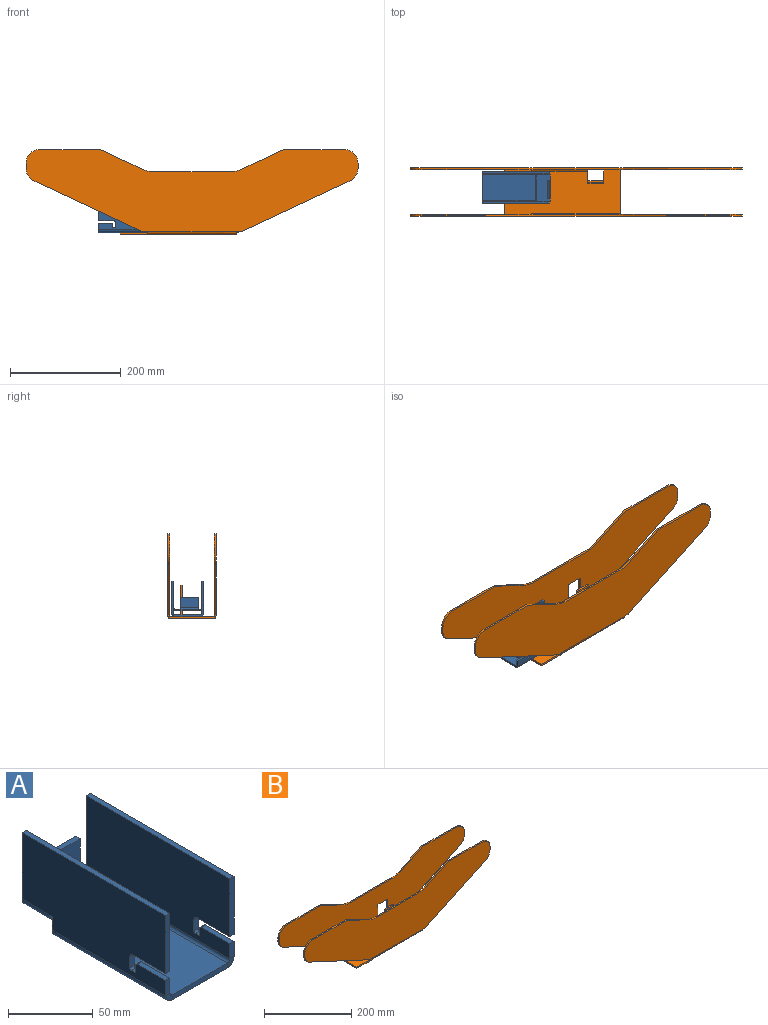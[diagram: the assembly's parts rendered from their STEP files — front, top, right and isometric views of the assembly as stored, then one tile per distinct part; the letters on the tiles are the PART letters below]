
ASSEMBLY  parts=2 mates=1
PART A: 69 faces, bbox 57x123.5x63.5 mm
  f0: cylinder r=1.5mm len=3.5mm, axis (1,0,0), area 8.2mm2, adj f1,f14,f15,f16
  f1: plane 4.5x3.5mm, normal (0,1,0), area 15.7mm2, adj f0,f2,f15,f16
  f2: cylinder r=1mm len=3.5mm, axis (1,0,0), area 5.5mm2, adj f1,f3,f15,f16
  f3: plane 3.5x3mm, normal (0,0,1), area 10.5mm2, adj f2,f4,f15,f16
  f4: cylinder r=1mm len=3.5mm, axis (1,0,0), area 5.5mm2, adj f3,f5,f15,f16
  f5: plane 8x3.5mm, normal (0,-1,0), area 28mm2, adj f4,f6,f15,f16
  f6: cylinder r=3mm len=3.5mm, axis (1,0,0), area 16.5mm2, adj f5,f7,f15,f16
  f7: plane 27x3.5mm, normal (0,0,-1), area 94.5mm2, adj f6,f8,f15,f16
  f8: plane 41.92x3.5mm, normal (0,-1,0), area 146.7mm2, adj f7,f9,f15,f16
  f9: plane 120x3.5mm, normal (0,0,1), area 420mm2, adj f8,f10,f15,f16
  f10: plane 48x3.5mm, normal (0,1,0), area 168mm2, adj f9,f15,f16,f66
  f11: plane 3.5x2mm, normal (0,0,-1), area 7mm2, adj f12,f15,f16,f65
  f12: plane 10x3.5mm, normal (0,1,0), area 35mm2, adj f11,f15,f16,f43
  f13: plane 11.08x3.5mm, normal (0,-1,0), area 38.8mm2, adj f14,f15,f16,f44
  f14: plane 23.5x3.5mm, normal (0,0,1), area 82.2mm2, adj f0,f13,f15,f16
  f15: plane 120x58mm, normal (-1,0,0), area 6526.9mm2, adj f0,f1,f2,f3,f4,f5,f6,f7
  f16: plane 120x58mm, normal (1,0,0), area 6526.9mm2, adj f0,f1,f2,f3,f4,f5,f6,f7
  f17: cylinder r=3mm len=3.5mm, axis (1,0,0), area 16.5mm2, adj f18,f32,f33,f34
  f18: plane 8x3.5mm, normal (0,-1,0), area 28mm2, adj f17,f19,f33,f34
  f19: cylinder r=1mm len=3.5mm, axis (1,0,0), area 5.5mm2, adj f18,f20,f33,f34
  f20: plane 3.5x3mm, normal (0,0,1), area 10.5mm2, adj f19,f21,f33,f34
  f21: cylinder r=1mm len=3.5mm, axis (1,0,0), area 5.5mm2, adj f20,f22,f33,f34
  f22: plane 4.5x3.5mm, normal (0,1,0), area 15.7mm2, adj f21,f23,f33,f34
  f23: cylinder r=1.5mm len=3.5mm, axis (1,0,0), area 8.2mm2, adj f22,f24,f33,f34
  f24: plane 23.5x3.5mm, normal (0,0,1), area 82.2mm2, adj f23,f25,f33,f34
  f25: plane 11.08x3.5mm, normal (0,-1,0), area 38.8mm2, adj f24,f33,f34,f40
  f26: plane 8.05x3.5mm, normal (0,1,0), area 28.2mm2, adj f27,f33,f34,f39
  f27: plane 3.5x2mm, normal (0,0,-1), area 7mm2, adj f26,f28,f33,f34
  f28: plane 23x3.5mm, normal (0,0,-1), area 80.5mm2, adj f27,f29,f33,f34
  f29: plane 49.95x3.5mm, normal (0,1,0), area 174.8mm2, adj f28,f30,f33,f34
  f30: plane 120x3.5mm, normal (0,0,1), area 420mm2, adj f29,f31,f33,f34
  f31: plane 41.92x3.5mm, normal (0,-1,0), area 146.7mm2, adj f30,f32,f33,f34
  f32: plane 27x3.5mm, normal (0,0,-1), area 94.5mm2, adj f17,f31,f33,f34
  f33: plane 120x58mm, normal (1,0,0), area 6575.6mm2, adj f17,f18,f19,f20,f21,f22,f23,f24
  f34: plane 120x58mm, normal (-1,0,0), area 6575.6mm2, adj f17,f18,f19,f20,f21,f22,f23,f24
  f35: plane 46x3.5mm, normal (0,-1,0), area 161mm2, adj f37,f38,f40,f44
  f36: plane 46x3.5mm, normal (0,1,0), area 161mm2, adj f37,f38,f39,f43
  f37: plane 95x46mm, normal (0,0,-1), area 4370mm2, adj f35,f36,f41,f45
  f38: plane 95x46mm, normal (0,0,1), area 4370mm2, adj f35,f36,f42,f46
  f39: plane 5.5x5.5mm, normal (0,1,0), area 20.6mm2, adj f26,f36,f41,f42
  f40: plane 5.5x5.5mm, normal (0,-1,0), area 20.6mm2, adj f25,f35,f41,f42
  f41: cylinder r=5.5mm len=95mm, axis (0,1,0), area 820.7mm2, adj f33,f37,f39,f40
  f42: cylinder r=2mm len=95mm, axis (0,1,0), area 298.5mm2, adj f34,f38,f39,f40
  f43: plane 5.5x5.5mm, normal (0,1,0), area 20.6mm2, adj f12,f36,f45,f46
  f44: plane 5.5x5.5mm, normal (0,-1,0), area 20.6mm2, adj f13,f35,f45,f46
  f45: cylinder r=5.5mm len=95mm, axis (0,1,0), area 820.7mm2, adj f15,f37,f43,f44
  f46: cylinder r=2mm len=95mm, axis (0,1,0), area 298.5mm2, adj f16,f38,f43,f44
  f47: plane 3.75x1.48mm, normal (-1,0,0), area 1.7mm2, adj f49,f54,f63
  f48: plane 3.75x1.48mm, normal (1,0,0), area 1.7mm2, adj f53,f54,f63
  f49: plane 5x3.5mm, normal (0,1,0), area 17.5mm2, adj f47,f50,f54,f55,f62
  f50: plane 3.5x1.75mm, normal (1,0,0), area 6.1mm2, adj f49,f51,f54,f55
  f51: plane 23x3.5mm, normal (1,0,0), area 80.5mm2, adj f50,f52,f54,f55
  f52: plane 47.95x3.5mm, normal (0,-1,0), area 167.8mm2, adj f51,f54,f55,f65
  f53: plane 10x3.5mm, normal (0,1,0), area 35mm2, adj f48,f54,f55,f56,f66
  f54: plane 47.95x24.75mm, normal (0,0,-1), area 1063.2mm2, adj f47,f48,f49,f50,f51,f52,f53,f63
  f55: plane 47.95x24.75mm, normal (0,0,1), area 1063.2mm2, adj f49,f50,f51,f52,f53,f56,f62,f64
  f56: plane 5.5x4.02mm, normal (-1,0,0), area 9.2mm2, adj f53,f55,f58,f63,f64
  f57: plane 19.5x3.5mm, normal (1,0,0), area 68.3mm2, adj f59,f60,f61,f62
  f58: plane 19.5x3.5mm, normal (-1,0,0), area 68.3mm2, adj f56,f59,f60,f61
  f59: plane 32.95x3.5mm, normal (0,0,1), area 115.3mm2, adj f57,f58,f60,f61
  f60: plane 32.95x19.5mm, normal (0,1,0), area 642.5mm2, adj f57,f58,f59,f63
  f61: plane 32.95x19.5mm, normal (0,-1,0), area 642.5mm2, adj f57,f58,f59,f64
  f62: plane 5.5x4.02mm, normal (1,0,0), area 9.2mm2, adj f49,f55,f57,f63,f64
  f63: cylinder r=5.5mm len=32.95mm, axis (1,0,0), area 284.7mm2, adj f47,f48,f54,f56,f60,f62
  f64: cylinder r=2mm len=32.95mm, axis (1,0,0), area 103.5mm2, adj f55,f56,f61,f62
  f65: plane 5.5x5.5mm, normal (0,-1,0), area 20.6mm2, adj f11,f52,f67,f68
  f66: bspline ~5.5x5.5mm, area 21.5mm2, adj f10,f53,f67,f68
  f67: cylinder r=5.5mm len=24.75mm, axis (0,-1,0), area 206.3mm2, adj f15,f54,f65,f66
  f68: cylinder r=2mm len=24.75mm, axis (0,-1,0), area 75mm2, adj f16,f55,f65,f66
PART B: 75 faces, bbox 600x87x153.5 mm
  f0: plane 9.8x3.5mm, normal (0,0,-1), area 34.3mm2, adj f1,f3,f4,f72
  f1: plane 600x148mm, normal (0,1,0), area 58035mm2, adj f0,f2,f4,f5,f6,f7,f8,f9
  f2: cylinder r=25mm len=3.5mm, axis (0,1,0), area 2.9mm2, adj f1,f3,f10,f11
  f3: plane 600x148mm, normal (0,-1,0), area 58035mm2, adj f0,f2,f4,f5,f6,f7,f8,f9
  f4: cylinder r=25mm len=3.5mm, axis (0,1,0), area 2.9mm2, adj f0,f1,f3,f9
  f5: plane 109.22x3.5mm, normal (0,0,1), area 382.3mm2, adj f1,f3,f6,f20
  f6: cylinder r=25mm len=25mm, axis (0,1,0), area 137.4mm2, adj f1,f3,f5,f7
  f7: plane 9.07x3.5mm, normal (-1,0,0), area 31.8mm2, adj f1,f3,f6,f8
  f8: cylinder r=25mm len=22.66mm, axis (0,1,0), area 99.3mm2, adj f1,f3,f7,f9
  f9: plane 194.99x90.93mm, normal (-0.42,0,-0.91), area 753mm2, adj f1,f3,f4,f8
  f10: plane 9.8x3.5mm, normal (0,0,-1), area 34.3mm2, adj f1,f2,f3,f71
  f11: plane 194.99x90.93mm, normal (0.42,0,-0.91), area 753mm2, adj f1,f2,f3,f12
  f12: cylinder r=25mm len=22.66mm, axis (0,1,0), area 99.3mm2, adj f1,f3,f11,f13
  f13: plane 9.07x3.5mm, normal (1,0,0), area 31.8mm2, adj f1,f3,f12,f14
  f14: cylinder r=25mm len=25mm, axis (0,1,0), area 137.4mm2, adj f1,f3,f13,f15
  f15: plane 109.22x3.5mm, normal (0,0,1), area 382.3mm2, adj f1,f3,f14,f16
  f16: plane 75.73x35.32mm, normal (-0.42,0,0.91), area 292.5mm2, adj f1,f3,f15,f17
  f17: cylinder r=50mm len=21.13mm, axis (0,1,0), area 76.4mm2, adj f1,f3,f16,f18
  f18: plane 137.83x3.5mm, normal (0,0,1), area 482.4mm2, adj f1,f3,f17,f19
  f19: cylinder r=50mm len=21.13mm, axis (0,1,0), area 76.4mm2, adj f1,f3,f18,f20
  f20: plane 75.73x35.32mm, normal (0.42,0,0.91), area 292.5mm2, adj f1,f3,f5,f19
  f21: plane 3.75x1.48mm, normal (1,0,0), area 1.7mm2, adj f25,f32,f60
  f22: plane 3.75x1.48mm, normal (1,0,0), area 1.7mm2, adj f23,f32,f73
  f23: plane 50x3.5mm, normal (0,-1,0), area 175mm2, adj f22,f24,f32,f33,f72
  f24: plane 83.5x3.5mm, normal (-1,0,0), area 292.2mm2, adj f23,f25,f32,f33
  f25: plane 50x3.5mm, normal (0,1,0), area 175mm2, adj f21,f24,f32,f33,f34
  f26: plane 22.7x3.5mm, normal (1,0,0), area 79.4mm2, adj f27,f32,f33,f59
  f27: plane 3.5x1mm, normal (0,1,0), area 3.5mm2, adj f26,f32,f33,f68
  f28: plane 3.5x1mm, normal (0,1,0), area 3.5mm2, adj f29,f32,f33,f67
  f29: plane 24.65x3.5mm, normal (-1,0,0), area 86.3mm2, adj f28,f30,f32,f33
  f30: plane 29.46x3.5mm, normal (0,1,0), area 103.1mm2, adj f29,f31,f32,f33
  f31: plane 77.95x3.5mm, normal (1,0,0), area 272.8mm2, adj f30,f32,f33,f71
  f32: plane 210.01x83.5mm, normal (0,0,-1), area 15712.5mm2, adj f21,f22,f23,f24,f25,f26,f27,f28
  f33: plane 210.01x83.5mm, normal (0,0,1), area 15712.5mm2, adj f23,f24,f25,f26,f27,f28,f29,f30
  f34: plane 5.5x4.02mm, normal (-1,0,0), area 9.2mm2, adj f25,f33,f52,f60,f61
  f35: plane 600x149.95mm, normal (0,1,0), area 56365.6mm2, adj f36,f38,f39,f40,f41,f42,f43,f44
  f36: cylinder r=25mm len=8.99mm, axis (0,1,0), area 32.6mm2, adj f35,f37,f47,f48
  f37: plane 600x149.95mm, normal (0,-1,0), area 56365.6mm2, adj f36,f38,f39,f40,f41,f42,f43,f44
  f38: cylinder r=25mm len=3.5mm, axis (0,1,0), area 2.9mm2, adj f35,f37,f52,f53
  f39: cylinder r=50mm len=21.13mm, axis (0,1,0), area 76.4mm2, adj f35,f37,f40,f58
  f40: plane 137.83x3.5mm, normal (0,0,1), area 482.4mm2, adj f35,f37,f39,f41
  f41: cylinder r=50mm len=21.13mm, axis (0,1,0), area 76.4mm2, adj f35,f37,f40,f42
  f42: plane 75.73x35.32mm, normal (-0.42,0,0.91), area 292.5mm2, adj f35,f37,f41,f43
  f43: plane 109.22x3.5mm, normal (0,0,1), area 382.3mm2, adj f35,f37,f42,f44
  f44: cylinder r=25mm len=25mm, axis (0,1,0), area 137.4mm2, adj f35,f37,f43,f45
  f45: plane 9.07x3.5mm, normal (1,0,0), area 31.8mm2, adj f35,f37,f44,f46
  f46: cylinder r=25mm len=22.66mm, axis (0,1,0), area 99.3mm2, adj f35,f37,f45,f47
  f47: plane 194.99x90.93mm, normal (0.42,0,-0.91), area 753mm2, adj f35,f36,f37,f46
  f48: plane 31.04x3.5mm, normal (0,0,-1), area 108.6mm2, adj f35,f36,f37,f49
  f49: plane 59.95x3.5mm, normal (-1,0,0), area 209.8mm2, adj f35,f37,f48,f50
  f50: plane 30x3.5mm, normal (0,0,-1), area 105mm2, adj f35,f37,f49,f51
  f51: plane 58x3.5mm, normal (1,0,0), area 203mm2, adj f35,f37,f50,f59
  f52: plane 9.8x3.5mm, normal (0,0,-1), area 34.3mm2, adj f34,f35,f37,f38
  f53: plane 194.99x90.93mm, normal (-0.42,0,-0.91), area 753mm2, adj f35,f37,f38,f54
  f54: cylinder r=25mm len=22.66mm, axis (0,1,0), area 99.3mm2, adj f35,f37,f53,f55
  f55: plane 9.07x3.5mm, normal (-1,0,0), area 31.8mm2, adj f35,f37,f54,f56
  f56: cylinder r=25mm len=25mm, axis (0,1,0), area 137.4mm2, adj f35,f37,f55,f57
  f57: plane 109.22x3.5mm, normal (0,0,1), area 382.3mm2, adj f35,f37,f56,f58
  f58: plane 75.73x35.32mm, normal (0.42,0,0.91), area 292.5mm2, adj f35,f37,f39,f57
  f59: plane 5.5x5.5mm, normal (1,0,0), area 20.6mm2, adj f26,f51,f60,f61
  f60: cylinder r=5.5mm len=100.56mm, axis (1,0,0), area 868.7mm2, adj f21,f32,f34,f35,f59
  f61: cylinder r=2mm len=100.56mm, axis (1,0,0), area 315.9mm2, adj f33,f34,f37,f59
  f62: plane 54.5x3.5mm, normal (1,0,0), area 190.8mm2, adj f64,f65,f66,f67
  f63: plane 54.5x3.5mm, normal (-1,0,0), area 190.8mm2, adj f64,f65,f66,f68
  f64: plane 28x3.5mm, normal (0,0,1), area 98mm2, adj f62,f63,f65,f66
  f65: plane 54.5x28mm, normal (0,1,0), area 1526mm2, adj f62,f63,f64,f69
  f66: plane 54.5x28mm, normal (0,-1,0), area 1526mm2, adj f62,f63,f64,f70
  f67: plane 5.5x5.5mm, normal (1,0,0), area 20.6mm2, adj f28,f62,f69,f70
  f68: plane 5.5x5.5mm, normal (-1,0,0), area 20.6mm2, adj f27,f63,f69,f70
  f69: cylinder r=5.5mm len=28mm, axis (1,0,0), area 241.9mm2, adj f32,f65,f67,f68
  f70: cylinder r=2mm len=28mm, axis (1,0,0), area 88mm2, adj f33,f66,f67,f68
  f71: plane 5.5x5.5mm, normal (1,0,0), area 20.6mm2, adj f10,f31,f73,f74
  f72: plane 5.5x4.02mm, normal (-1,0,0), area 9.2mm2, adj f0,f23,f33,f73,f74
  f73: cylinder r=5.5mm len=160.01mm, axis (1,0,0), area 1382.4mm2, adj f3,f22,f32,f71,f72
  f74: cylinder r=2mm len=160.01mm, axis (1,0,0), area 502.7mm2, adj f1,f33,f71,f72
PLACE A rot(axis=(0,0,-1),90deg) t=(-169.82,11.8,222.77)mm
PLACE B t=(-55.67,-21.15,169.53)mm
MATE planar A.f37 <-> B.f33  axis (0,0,-1) through (-176.91,-13.2,169.53)mm
